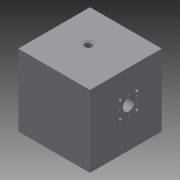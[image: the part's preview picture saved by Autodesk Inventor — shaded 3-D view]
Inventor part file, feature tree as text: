
AUTODESK INVENTOR PART (.ipt)
format: ipt  version: 2014 (Build 180170000, 170)  size: 288,768 bytes
history: native  units: mm
features: other x50, sketch x3, extrude x1
ambient origin geometry x8: Origin, YZ Plane, XZ Plane, XY Plane, X Axis, Y Axis, Z Axis, Center Point
bodies: 实体1 (feature_tree)
feature tree (54):
  extrude  "拉伸1"  TaperAngle=0.0deg  [1 undecoded]
  other  "UCS1"
  other  "UCS2"
  other  "UCS3"
  other  "UCS4"
  other  "UCS5"
  other  "UCS6"
  other  "iFeature4:2"
  other  "iFeature4:1"
  sketch  "草图1"  dims[d0=200.0mm d1=0.0mm]
  other  "UCS1: YZ 平面"
  other  "UCS1: XZ 平面"
  other  "UCS1: XY 平面"
  other  "UCS1: X 轴"
  other  "UCS1: Y 轴"
  other  "UCS1: Z 轴"
  other  "UCS1: 原点"
  other  "UCS2: YZ 平面"
  other  "UCS2: XZ 平面"
  other  "UCS2: XY 平面"
  other  "UCS2: X 轴"
  other  "UCS2: Y 轴"
  other  "UCS2: Z 轴"
  other  "UCS2: 原点"
  other  "UCS3: YZ 平面"
  other  "UCS3: XZ 平面"
  other  "UCS3: XY 平面"
  other  "UCS3: X 轴"
  other  "UCS3: Y 轴"
  other  "UCS3: Z 轴"
  other  "UCS3: 原点"
  other  "UCS4: YZ 平面"
  other  "UCS4: XZ 平面"
  other  "UCS4: XY 平面"
  other  "UCS4: X 轴"
  other  "UCS4: Y 轴"
  other  "UCS4: Z 轴"
  other  "UCS4: 原点"
  other  "UCS5: YZ 平面"
  other  "UCS5: XZ 平面"
  other  "UCS5: XY 平面"
  other  "UCS5: X 轴"
  other  "UCS5: Y 轴"
  other  "UCS5: Z 轴"
  other  "UCS5: 原点"
  other  "UCS6: YZ 平面"
  other  "UCS6: XZ 平面"
  other  "UCS6: XY 平面"
  other  "UCS6: X 轴"
  other  "UCS6: Y 轴"
  other  "UCS6: Z 轴"
  other  "UCS6: 原点"
  sketch  "草图4"  dims[d2=0.0mm d3=0.0mm d4=0.0mm d5=0.0mm d6=0.0mm d7=0.0mm]
  sketch  "草图6"  dims[d8=0.0mm d9=0.0mm d10=0.0mm d11=0.0mm d12=0.0mm d13=0.0mm d14=0.0mm d15=0.0mm d16=0.0mm d17=0.0mm d18=0.0mm d19=0.0mm d20=0.0mm d21=0.0mm d22=0.0mm d23=0.0mm d24=0.0mm d25=0.0mm d26=0.0mm d27=0.0mm d28=0.0mm d29=0.0mm d30=0.0mm d31=0.0mm d32=0.0mm d33=0.0mm d34=0.0mm d35=0.0mm d36=0.0mm d37=0.0mm d38=0.0mm d39=0.0mm d40=0.0mm d41=0.0mm d50=0.0mm d54=-17.0mm d55=0.0mm d59=-17.0mm d60=0.0mm d78=0.0mm]
note: 1 required parameter value undecoded (feature->parameter linkage not recoverable at this tier; creation-order binding heuristic only, values carry confidence <= 0.55)
